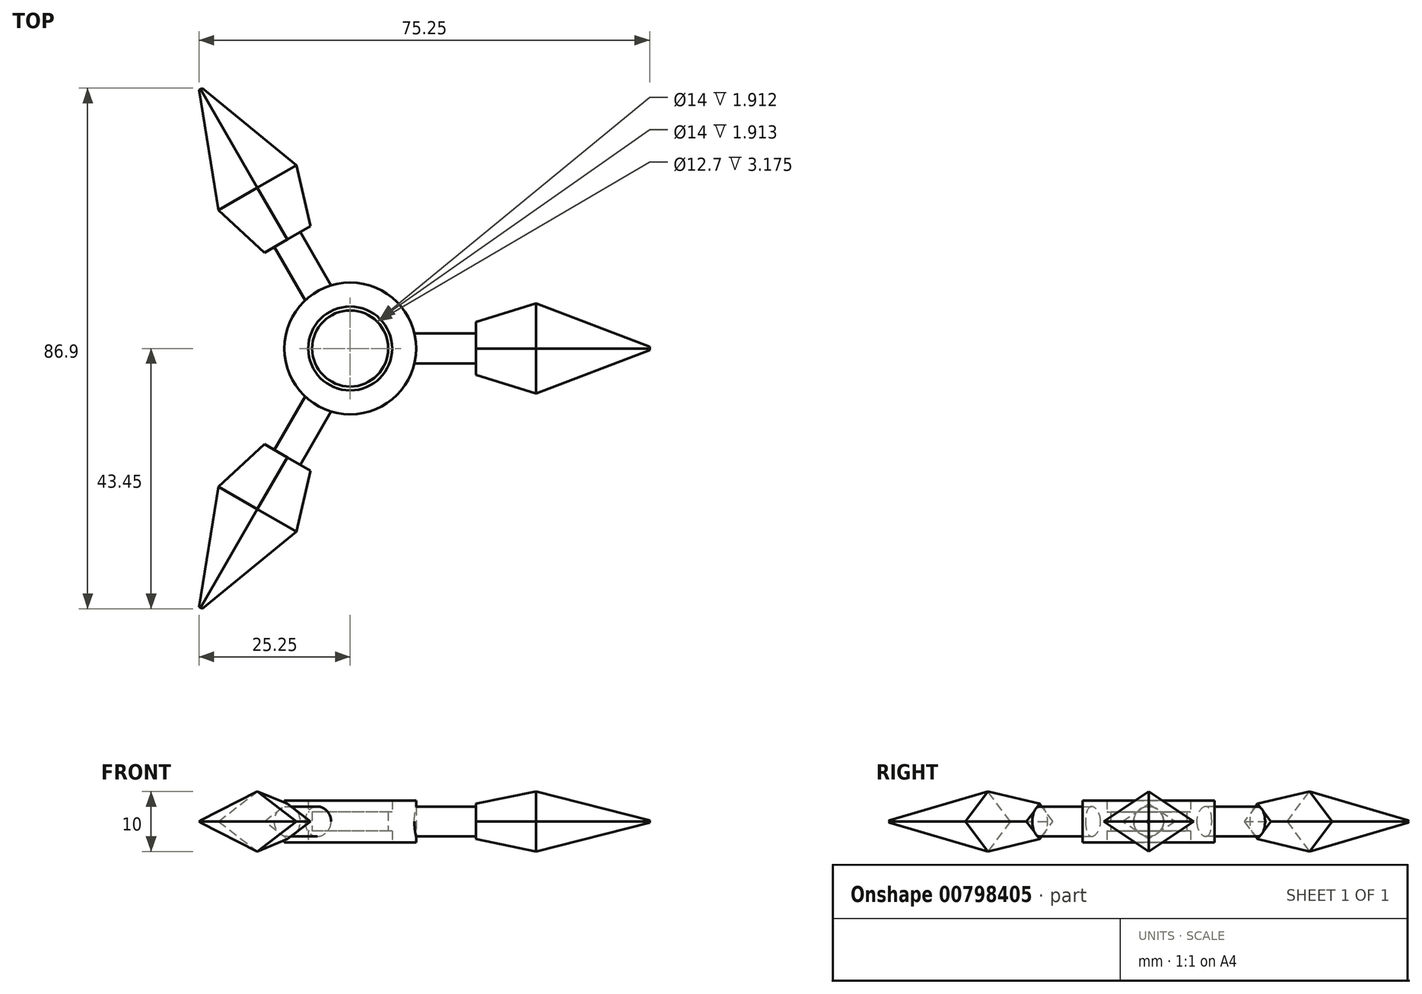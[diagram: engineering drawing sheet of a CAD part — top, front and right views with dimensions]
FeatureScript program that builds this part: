
annotation { "Feature Type Name" : "Feature", "Feature Type Description" : "" }
export const myFeature = defineFeature(function(context is Context, id is Id, definition is map)
    precondition{}
    {
        {
            var Q0;
            Q0=qCreatedBy(makeId("Top.planeOp"),FACE);
            var sketch = newSketch(context, id + "F0", { "sketchPlane" : qUnion([Q0])});
            skCircle(sketch, "E0", {"center": v(0, 0) * mm, "radius": 11 * mm});
            skLineSegment(sketch, "E1.bottom", {"start": v(10.71, 2.5) * mm, "end": v(21, 2.5) * mm});
            skLineSegment(sketch, "E1.top", {"start": v(10.71, -2.5) * mm, "end": v(21, -2.5) * mm});
            skLineSegment(sketch, "E1.left", {"start": v(10.71, 2.5) * mm, "end": v(10.71, -2.5) * mm});
            skLineSegment(sketch, "E1.right", {"start": v(21, 2.5) * mm, "end": v(21, -2.5) * mm});
            skLineSegment(sketch, "E2", {"start": v(21, 2.5) * mm, "end": v(31, 7.5) * mm});
            skLineSegment(sketch, "E3", {"start": v(31, 7.5) * mm, "end": v(31, 7.5) * mm});
            skLineSegment(sketch, "E4", {"start": v(50, 0) * mm, "end": v(31, 7.5) * mm});
            skLineSegment(sketch, "E5", {"start": v(50, 0) * mm, "end": v(31, -7.5) * mm});
            skLineSegment(sketch, "E6", {"start": v(31, -7.5) * mm, "end": v(21, -2.5) * mm});
            skCircle(sketch, "E7", {"center": v(0, 0) * mm, "radius": 7 * mm});
            skLineSegment(sketch, "E8", {"start": v(0, 0) * mm, "end": v(50, 0) * mm, "construction": true});
            skLineSegment(sketch, "E9.bottom", {"start": v(21, 7.5) * mm, "end": v(50, 7.5) * mm});
            skLineSegment(sketch, "E9.top", {"start": v(21, -7.5) * mm, "end": v(50, -7.5) * mm});
            skLineSegment(sketch, "E9.left", {"start": v(21, 7.5) * mm, "end": v(21, -7.5) * mm});
            skLineSegment(sketch, "E9.right", {"start": v(50, 7.5) * mm, "end": v(50, -7.5) * mm});
            skCircle(sketch, "E10", {"center": v(0, 0) * mm, "radius": 6.35 * mm});
            skSolve(sketch);
        }
        {
            var Q0;
            {var subQ0=sQuery(id+"F0.wireOp",EDGE,"E1.left");Q0=makeQuery(id+"F0.imprint","IMPRINT",FACE,{"disambiguationData":[TD([[makeQuery(id+"F0.imprint","IMPRINT",EDGE,{"derivedFrom":subQ0}),-1.0]])]});}
            var Q1;
            {var subQ0=sQuery(id+"F0.wireOp",EDGE,"E1.left");Q1=makeQuery(id+"F0.imprint","IMPRINT",FACE,{"disambiguationData":[TD([[makeQuery(id+"F0.imprint","IMPRINT",EDGE,{"derivedFrom":subQ0}),1.0]])]});}
            extrude(context, id + "F1", {"entities" : qUnion([Q0, Q1]), "endBound" : BoundingType.SYMMETRIC, "depth" : 7 * mm, "offsetDistance" : 25 * mm});
        }
        {
            var Q0;
            {var subQ1=sQuery(id+"F0.wireOp",EDGE,"E2");Q0=makeQuery(id+"F0.imprint","IMPRINT",FACE,{"disambiguationData":[TD([[makeQuery(id+"F0.imprint","IMPRINT",EDGE,{"derivedFrom":subQ1}),-1.0]])]});}
            var Q1;
            {var subQ0=sQuery(id+"F0.wireOp",EDGE,"E2");Q1=makeQuery(id+"F0.imprint","IMPRINT",FACE,{"disambiguationData":[TD([[makeQuery(id+"F0.imprint","IMPRINT",EDGE,{"derivedFrom":subQ0}),1.0]])]});}
            var Q2;
            {var subQ0=sQuery(id+"F0.wireOp",EDGE,"E6");Q2=makeQuery(id+"F0.imprint","IMPRINT",FACE,{"disambiguationData":[TD([[makeQuery(id+"F0.imprint","IMPRINT",EDGE,{"derivedFrom":subQ0}),1.0]])]});}
            var Q3;
            {var subQ0=sQuery(id+"F0.wireOp",EDGE,"E4");Q3=makeQuery(id+"F0.imprint","IMPRINT",FACE,{"disambiguationData":[TD([[makeQuery(id+"F0.imprint","IMPRINT",EDGE,{"derivedFrom":subQ0}),-1.0]])]});}
            var Q4;
            {var subQ0=sQuery(id+"F0.wireOp",EDGE,"E5");Q4=makeQuery(id+"F0.imprint","IMPRINT",FACE,{"disambiguationData":[TD([[makeQuery(id+"F0.imprint","IMPRINT",EDGE,{"derivedFrom":subQ0}),1.0]])]});}
            extrude(context, id + "F2", {"entities" : qUnion([Q0, Q1, Q2, Q3, Q4]), "endBound" : BoundingType.SYMMETRIC, "depth" : 10 * mm, "offsetDistance" : 25 * mm});
        }
        {
            var Q0;
            Q0=makeQuery(id+"F2.opExtrude","CAP_EDGE",EDGE,{"disambiguationData":[OSD([sQuery(id+"F0.wireOp",EDGE,"E9.bottom")])],"isStart":false});
            var Q1;
            Q1=makeQuery(id+"F2.opExtrude","CAP_EDGE",EDGE,{"disambiguationData":[OSD([sQuery(id+"F0.wireOp",EDGE,"E9.top")])],"isStart":true});
            var Q2;
            Q2=makeQuery(id+"F2.opExtrude","CAP_EDGE",EDGE,{"disambiguationData":[OSD([sQuery(id+"F0.wireOp",EDGE,"E9.top")])],"isStart":false});
            var Q3;
            Q3=makeQuery(id+"F2.opExtrude","CAP_EDGE",EDGE,{"disambiguationData":[OSD([sQuery(id+"F0.wireOp",EDGE,"E9.bottom")])],"isStart":true});
            chamfer(context, id + "F3", {"entities" : qUnion([Q0, Q1, Q2, Q3]), "chamferType" : ChamferType.TWO_OFFSETS, "width1" : 5 * mm, "oppositeDirection" : false, "width2" : 7.5 * mm, "tangentPropagation" : true});
        }
        {
            var Q0;
            Q0=makeQuery(id+"F3.opChamfer","BLEND_EDGE",EDGE,{"blendedFrom":[makeQuery(id+"F2.opExtrude","CAP_EDGE",EDGE,{"disambiguationData":[OSD([sQuery(id+"F0.wireOp",EDGE,"E9.bottom")])],"isStart":false}),makeQuery(id+"F2.opExtrude","SWEPT_FACE",FACE,{"disambiguationData":[OSD([sQuery(id+"F0.wireOp",EDGE,"E9.right")])]})],"blendedInto":[makeQuery(id+"F2.opExtrude","SWEPT_FACE",FACE,{"disambiguationData":[OSD([sQuery(id+"F0.wireOp",EDGE,"E9.right")])]})]});
            var Q1;
            Q1=makeQuery(id+"F3.opChamfer","BLEND_EDGE",EDGE,{"blendedFrom":[makeQuery(id+"F2.opExtrude","CAP_EDGE",EDGE,{"disambiguationData":[OSD([sQuery(id+"F0.wireOp",EDGE,"E9.top")])],"isStart":false}),makeQuery(id+"F2.opExtrude","SWEPT_FACE",FACE,{"disambiguationData":[OSD([sQuery(id+"F0.wireOp",EDGE,"E9.right")])]})],"blendedInto":[makeQuery(id+"F2.opExtrude","SWEPT_FACE",FACE,{"disambiguationData":[OSD([sQuery(id+"F0.wireOp",EDGE,"E9.right")])]})]});
            var Q2;
            Q2=makeQuery(id+"F3.opChamfer","BLEND_EDGE",EDGE,{"blendedFrom":[makeQuery(id+"F2.opExtrude","CAP_EDGE",EDGE,{"disambiguationData":[OSD([sQuery(id+"F0.wireOp",EDGE,"E9.top")])],"isStart":true}),makeQuery(id+"F2.opExtrude","SWEPT_FACE",FACE,{"disambiguationData":[OSD([sQuery(id+"F0.wireOp",EDGE,"E9.right")])]})],"blendedInto":[makeQuery(id+"F2.opExtrude","SWEPT_FACE",FACE,{"disambiguationData":[OSD([sQuery(id+"F0.wireOp",EDGE,"E9.right")])]})]});
            var Q3;
            Q3=makeQuery(id+"F3.opChamfer","BLEND_EDGE",EDGE,{"blendedFrom":[makeQuery(id+"F2.opExtrude","CAP_EDGE",EDGE,{"disambiguationData":[OSD([sQuery(id+"F0.wireOp",EDGE,"E9.bottom")])],"isStart":true}),makeQuery(id+"F2.opExtrude","SWEPT_FACE",FACE,{"disambiguationData":[OSD([sQuery(id+"F0.wireOp",EDGE,"E9.right")])]})],"blendedInto":[makeQuery(id+"F2.opExtrude","SWEPT_FACE",FACE,{"disambiguationData":[OSD([sQuery(id+"F0.wireOp",EDGE,"E9.right")])]})]});
            chamfer(context, id + "F4", {"entities" : qUnion([Q0, Q1, Q2, Q3]), "chamferType" : ChamferType.TWO_OFFSETS, "width1" : 4 * mm, "oppositeDirection" : false, "width2" : 19 * mm, "tangentPropagation" : true});
        }
        {
            var Q0;
            Q0=makeQuery(id+"F3.opChamfer","BLEND_EDGE",EDGE,{"blendedFrom":[makeQuery(id+"F2.opExtrude","CAP_EDGE",EDGE,{"disambiguationData":[OSD([sQuery(id+"F0.wireOp",EDGE,"E9.bottom")])],"isStart":false}),makeQuery(id+"F2.opExtrude","SWEPT_FACE",FACE,{"disambiguationData":[OSD([sQuery(id+"F0.wireOp",EDGE,"E9.left")])]})],"blendedInto":[makeQuery(id+"F2.opExtrude","SWEPT_FACE",FACE,{"disambiguationData":[OSD([sQuery(id+"F0.wireOp",EDGE,"E9.left")])]})]});
            var Q1;
            Q1=makeQuery(id+"F3.opChamfer","BLEND_EDGE",EDGE,{"blendedFrom":[makeQuery(id+"F2.opExtrude","CAP_EDGE",EDGE,{"disambiguationData":[OSD([sQuery(id+"F0.wireOp",EDGE,"E9.top")])],"isStart":false}),makeQuery(id+"F2.opExtrude","SWEPT_FACE",FACE,{"disambiguationData":[OSD([sQuery(id+"F0.wireOp",EDGE,"E9.left")])]})],"blendedInto":[makeQuery(id+"F2.opExtrude","SWEPT_FACE",FACE,{"disambiguationData":[OSD([sQuery(id+"F0.wireOp",EDGE,"E9.left")])]})]});
            var Q2;
            Q2=makeQuery(id+"F3.opChamfer","BLEND_EDGE",EDGE,{"blendedFrom":[makeQuery(id+"F2.opExtrude","CAP_EDGE",EDGE,{"disambiguationData":[OSD([sQuery(id+"F0.wireOp",EDGE,"E9.bottom")])],"isStart":true}),makeQuery(id+"F2.opExtrude","SWEPT_FACE",FACE,{"disambiguationData":[OSD([sQuery(id+"F0.wireOp",EDGE,"E9.left")])]})],"blendedInto":[makeQuery(id+"F2.opExtrude","SWEPT_FACE",FACE,{"disambiguationData":[OSD([sQuery(id+"F0.wireOp",EDGE,"E9.left")])]})]});
            var Q3;
            Q3=makeQuery(id+"F3.opChamfer","BLEND_EDGE",EDGE,{"blendedFrom":[makeQuery(id+"F2.opExtrude","CAP_EDGE",EDGE,{"disambiguationData":[OSD([sQuery(id+"F0.wireOp",EDGE,"E9.top")])],"isStart":true}),makeQuery(id+"F2.opExtrude","SWEPT_FACE",FACE,{"disambiguationData":[OSD([sQuery(id+"F0.wireOp",EDGE,"E9.left")])]})],"blendedInto":[makeQuery(id+"F2.opExtrude","SWEPT_FACE",FACE,{"disambiguationData":[OSD([sQuery(id+"F0.wireOp",EDGE,"E9.left")])]})]});
            chamfer(context, id + "F5", {"entities" : qUnion([Q0, Q1, Q2, Q3]), "chamferType" : ChamferType.TWO_OFFSETS, "width1" : 1.7 * mm, "oppositeDirection" : false, "width2" : 10 * mm, "tangentPropagation" : true});
        }
        {
            var Q0;
            {var subQ1=sQuery(id+"F0.wireOp",EDGE,"E1.bottom");Q0=makeQuery(id+"F0.imprint","IMPRINT",FACE,{"disambiguationData":[TD([[makeQuery(id+"F0.imprint","IMPRINT",EDGE,{"derivedFrom":subQ1}),-1.0]])]});}
            extrude(context, id + "F6", {"entities" : qUnion([Q0]), "endBound" : BoundingType.SYMMETRIC, "depth" : 5 * mm, "offsetDistance" : 25 * mm});
        }
        {
            var Q0;
            Q0=makeQuery(id+"F6.opExtrude","CAP_EDGE",EDGE,{"disambiguationData":[OSD([sQuery(id+"F0.wireOp",EDGE,"E1.top")])],"isStart":false});
            var Q1;
            Q1=makeQuery(id+"F6.opExtrude","CAP_EDGE",EDGE,{"disambiguationData":[OSD([sQuery(id+"F0.wireOp",EDGE,"E1.bottom")])],"isStart":false});
            var Q2;
            Q2=makeQuery(id+"F6.opExtrude","CAP_EDGE",EDGE,{"disambiguationData":[OSD([sQuery(id+"F0.wireOp",EDGE,"E1.top")])],"isStart":true});
            var Q3;
            Q3=makeQuery(id+"F6.opExtrude","CAP_EDGE",EDGE,{"disambiguationData":[OSD([sQuery(id+"F0.wireOp",EDGE,"E1.bottom")])],"isStart":true});
            fillet(context, id + "F7", {"entities" : qUnion([Q0, Q1, Q2, Q3]), "radius" : 2.5 * mm, "tangentPropagation" : true, "allowEdgeOverflow" : false});
        }
        {
            var Q0;
            Q0=makeQuery(id+"F2.opExtrude","SWEPT_BODY",BODY,{"disambiguationData":[OSD([sQuery(id+"F0.wireOp",EDGE,"E9.bottom"),sQuery(id+"F0.wireOp",EDGE,"E9.top"),sQuery(id+"F0.wireOp",EDGE,"E9.left"),sQuery(id+"F0.wireOp",EDGE,"E9.right")])]});
            var Q1;
            Q1=makeQuery(id+"F6.opExtrude","SWEPT_BODY",BODY,{"disambiguationData":[OSD([sQuery(id+"F0.wireOp",EDGE,"E0"),sQuery(id+"F0.wireOp",EDGE,"E1.bottom"),sQuery(id+"F0.wireOp",EDGE,"E1.top"),sQuery(id+"F0.wireOp",EDGE,"E9.left")])]});
            var Q2;
            Q2=sQuery(id+"F0.wireOp",EDGE,"E7");
            circularPattern(context, id + "F8", {"entities" : qUnion([Q0, Q1]), "axis" : qUnion([Q2]), "angle" : 360 * degree, "instanceCount" : 3, "equalSpace" : true});
        }
        {
            var Q0;
            Q0=makeQuery(id+"F0.imprint","IMPRINT",FACE,{"disambiguationData":[TD([[makeQuery(id+"F0.imprint","IMPRINT",EDGE,{"derivedFrom":sQuery(id+"F0.wireOp",EDGE,"E7")}),1.0]])]});
            extrude(context, id + "F9", {"entities" : qUnion([Q0]), "operationType" : NewBodyOperationType.ADD, "endBound" : BoundingType.SYMMETRIC, "depth" : 3.17 * mm, "offsetDistance" : 25 * mm});
        }
    });
